# Revit family: Naveka VSEC
name_source: partatom
category: Оборудование
units: mm (PartAtom-declared; Revit-internal decimal feet)

## family parameters
Всегда вертикально = Да
Заголовок OmniClass = Climate Control (HVAC)
На основе рабочей плоскости = Нет
Номер OmniClass = 23.75.00.00
Общий = Нет
При загрузке вырезать с полостями = Нет
Размер круглого соединителя = Использовать диаметр
Тип детали = Нормальный
Точка расчета площади = Нет

## types (8) — shared parameters
ADSK_Единица измерения = шт.
ADSK_Завод-изготовитель = Naveka
ADSK_Наименование = Вентилятор шумоизолированный для прямоугольного канала
Материал = RAL 0000 Серый металл

## per-type parameters (varying)
| type | ADSK_Масса | B | B1 | Bm1 | H | H1 | Hm | Lm | Мощность двигателя N,Вт | Напряжение U,В | Сила тока J, А | Частота вращения n, об/мин |
| VSEC1-5025 | 28 | 500 мм | 520 мм | 580 мм | 250 мм | 270 мм | 380 мм | 430 мм | 170 | 1-220 | 1.4 | 2860 |
| VSEC1-5030 | 32 | 500 мм | 520 мм | 580 мм | 300 мм | 320 мм | 430 мм | 430 мм | 380 | 1-220 | 2.5 | 3370 |
| VSEC1-6030 | 41 | 600 мм | 620 мм | 680 мм | 300 мм | 320 мм | 468 мм | 600 мм | 660 | 1-220 | 2.9 | 2900 |
| VSEC1-6035 | 46 | 600 мм | 620 мм | 680 мм | 350 мм | 370 мм | 518 мм | 600 мм | 730 | 1-220 | 3.2 | 2640 |
| VSEC3-7040A | 62 | 700 мм | 730 мм | 780 мм | 400 мм | 430 мм | 560 мм | 670 мм | 1320 | 3-380 | 2.1 | 2060 |
| VSEC3-7040B | 92 | 700 мм | 730 мм | 780 мм | 500 мм | 430 мм | 650 мм | 750 мм | 3050 | 3-380 | 4.6 | 3230 |
| VSEC3-8050 | 113 | 800 мм | 830 мм | 880 мм | 500 мм | 530 мм | 760 мм | 850 мм | 3800 | 3-380 | 5.8 | 2800 |
| VSEC3-10050 | 145 | 1000 мм | 1030 мм | 1080 мм | 500 мм | 530 мм | 760 мм | 1000 мм | 4500 | 3-380 | 6.8 | 2480 |

note: column(s) folded — value = type name in every type: ADSK_Марка
